# Revit family: O3IM - All
name_source: partatom
category: Mechanical Equipment
units: mm (PartAtom-declared; Revit-internal decimal feet)

## family parameters
Always vertical = Yes
Cut with Voids When Loaded = No
OmniClass Number = 23.40.40.11.17
OmniClass Title = Refrigerated Cases
Part Type = Normal
Room Calculation Point = No
Round Connector Dimension = Use Radius
Shared = No
Work Plane-Based = Yes

## types (14) — shared parameters
12" Shelf = Yes
16" Shelf = Yes
BOTTOM ELECTRICAL = Yes
BOTTOM REFRIGERATION PIPING = Yes
Certifications = NSF 7, UL471, CSA
DATE = 03/29/2016
DRAIN PIPING = Yes
Default Elevation = 48"
Description = O3IM - Island case
EQUIPMENT DESCRIPTION = O3IM - Island case
EQUIPMENT MARK = O3IM
Ends = Yes
GLASS = Glass
Height = 53 1/4"
How Many Defrosts Per Day = 4
Island Anti-Condensate Heaters Amps = 1 A
Island Discharge Air Velocity (FPM) = 270 FPM
Island Electric Fail-Safe = 30 (Min)
Island Electric Termination Temp (F°) = 47 °F
Island Hot Gas Fail-Safe (Min) = 26 (Min)
Island Hot Gas Termination Temp (F°) = 45 °F
Island Run-Off Time (Min) = 6-8 (Min)
Island Superheat @ Bulb Set Point (°F) = 6-8 °F
Island Timed-Off Fail-Safe (Min) = 45 (Min)
Island Timed-Off Termination Temp (°F) = 45 °F
Item Description = O3IM - Island case
LF STD END = Yes
Legend Number = O3IM
Manufacturer = HILL PHOENIX
Model = O3IM
Number of Shelf = 3
PAINTED METAL UPPER SHELF = PAINTED SHELVES
REAR REFRIGERATION PIPING = Yes
REFRIGERATION PIPING = COPPER PIPE
RT STD END = Yes
Refgn = 8 5/8"
STAINLESS STEEL = GALVANIZED STEEL
Shelf distance = 48"
TOP ELECTRICAL = Yes
TOP REFRIGERATION PIPING = Yes
URL = http://www.hillphoenix.com
Width = 79 3/4"
zero-valued in all types: Island Fans Per Case

## per-type parameters (varying)
| type | CENTER LINE | Case End | High Power (Cornice) Amps | High Power (Cornice) Watts | Island  Case Length | Island 208V Defrost Heaters Amps | Island 208V Defrost Heaters Watts | Island 240 Defrost Heaters Amps | Island 240 Defrost Heaters Watts | Island Anti-Condensate Heaters Watts | Island Application | Island BTUH Conventional | Island BTUH Parallel | Island Discharge Air(°F) | Island Evaporator (°F) | Island High Efficiency Fans Amps | Island High Efficiency Fans Watts | Length | Light Length | Lights Per Row | Shelf Depth | Standard Power Amps | Standard Power Watts |
| 08' | 52 3/4" | 8' Wrapped | 1 A | 107 W | 96" | 8 A | 1600 A | 9 A | 2130 W | 80 W | Dairy / Deli / Produce | 1513 | 1366 | 30 °F | 22 °F | 0 A | 28 W | 105 1/2" | 2 (2ft), 2 (4ft) | 4 | Top Sill | 1 A | 59 W |
| 12' | 76 3/4" | 8' Wrapped | 1 A | 107 W | 96" | 8 A | 1600 A | 9 A | 2130 W | 80 W | Dairy / Deli / Produce | 1513 | 1366 | 30 °F | 22 °F | 0 A | 28 W | 153 1/2" | 2 (2ft), 2 (4ft) | 4 | Top Sill | 1 A | 59 W |
| 08' --- Top Sill - Deli | 52 3/4" | 8' Wrapped | 1 A | 107 W | 96" | 8 A | 1600 A | 9 A | 2130 W | 80 W | Dairy / Deli / Produce | 1513 | 1366 | 30 °F | 22 °F | 0 A | 28 W | 105 1/2" | 2 (2ft), 2 (4ft) | 4 | Top Sill | 1 A | 59 W |
| 08' ---  8" Shelf - Deli | 52 3/4" | 8' Wrapped | 1 A | 65 W | 96" | 8 A | 1600 A | 9 A | 2130 W | 80 W | Dairy / Deli / Produce | 1513 | 1366 | 30 °F | 22 °F | 0 A | 28 W | 105 1/2" | 2 (5ft), 2 (3ft) | 4 | 8" Shelves | 0 A | 37 W |
| 08' --- 10-16" Shelf - Meat | 52 3/4" | 8' Wrapped | 1 A | 70 W | 96" | 8 A | 1600 A | 9 A | 2130 W | 80 W | Meat | 1657 | 1496 | 26 °F | 17 °F | 0 A | 28 W | 105 1/2" | 2 (5ft), 4 (3ft) | 4 | 10-16" Shelves | 0 A | 39 W |
| 12' --- Top Sill - Deli | 76 3/4" | 12' Wrapped | 1 A | 107 W | 144" | 12 A | 2400 A | 13 A | 3200 W | 127 W | Dairy / Deli / Produce | 1513 | 1366 | 30 °F | 22 °F | 1 A | 37 W | 153 1/2" | 2 (2ft), 4 (4ft) | 6 | Top Sill | 1 A | 60 W |
| 12' ---  8" Shelf - Deli | 76 3/4" | 12' Wrapped | 1 A | 65 W | 144" | 12 A | 2400 A | 13 A | 3200 W | 127 W | Dairy / Deli / Produce | 1513 | 1366 | 30 °F | 22 °F | 1 A | 37 W | 153 1/2" | 2 (5ft), 4 (3ft) | 6 | 8" Shelves | 0 A | 37 W |
| 12' --- 10-16" Shelf - Deli | 76 3/4" | 12' | 0 A | 0 W | 144" | 12 A | 2400 A | 13 A | 3200 W | 127 W | Deli | 1513 | 1366 | 30 °F | 22 °F | 1 A | 37 W | 153 1/2" | 2 (1ft), 4 (3ft) | 6 | 10", 12", 14", 16" | 0 A | 23 W |
| 08' ---  8" Shelf - Meat | 52 3/4" | 8' Wrapped | 1 A | 65 W | 96" | 8 A | 1600 A | 9 A | 2130 W | 80 W | Meat | 1657 | 1496 | 17 °F | 26 °F | 0 A | 28 W | 105 1/2" | 2 (5ft), 2 (3ft) | 4 | 8" Shelves | 0 A | 37 W |
| 08' --- 10-16" Shelf - Deli | 52 3/4" | 12' | 0 A | 0 W | 96" | 8 A | 1600 A | 9 A | 2130 W | 80 W | Deli | 1513 | 1366 | 30 °F | 22 °F | 0 A | 28 W | 105 1/2" | 2 (1ft), 4 (3ft) | 6 | 10", 12", 14", 16" | 0 A | 23 W |
| 08' --- Top Sill - Meat | 52 3/4" | 8' Wrapped | 1 A | 107 W | 96" | 8 A | 1600 A | 9 A | 2130 W | 80 W | Meat | 1657 | 1496 | 26 °F | 17 °F | 0 A | 28 W | 105 1/2" | 2 (2ft), 2 (4ft) | 4 | Top Sill | 1 A | 59 W |
| 12' --- Top Sill - Meat | 76 3/4" | 12' Wrapped | 1 A | 107 W | 144" | 12 A | 2400 A | 13 A | 3200 W | 127 W | Meat | 1657 | 1496 | 26 °F | 17 °F | 1 A | 37 W | 153 1/2" | 2 (2ft), 4 (4ft) | 6 | Top Sill | 1 A | 60 W |
| 12' ---  8" Shelf - Meat | 76 3/4" | 12' Wrapped | 1 A | 65 W | 144" | 12 A | 2400 A | 13 A | 3200 W | 127 W | Meat | 1657 | 1496 | 26 °F | 17 °F | 1 A | 37 W | 153 1/2" | 2 (5ft), 4 (3ft) | 6 | 8" Shelves | 0 A | 37 W |
| 12' --- 10-16" Shelf - Meat | 76 3/4" | 12' Wrapped | 1 A | 70 W | 144" | 12 A | 2400 A | 13 A | 3200 W | 127 W | Meat | 1657 | 1496 | 26 °F | 17 °F | 1 A | 37 W | 153 1/2" | 2 (5ft), 4 (3ft) | 6 | 10-16" Shelves | 0 A | 39 W |

## geometry (parser evidence)
native form markers: Blend x8, Sweep x1
no freeform markers — native parametric forms only
